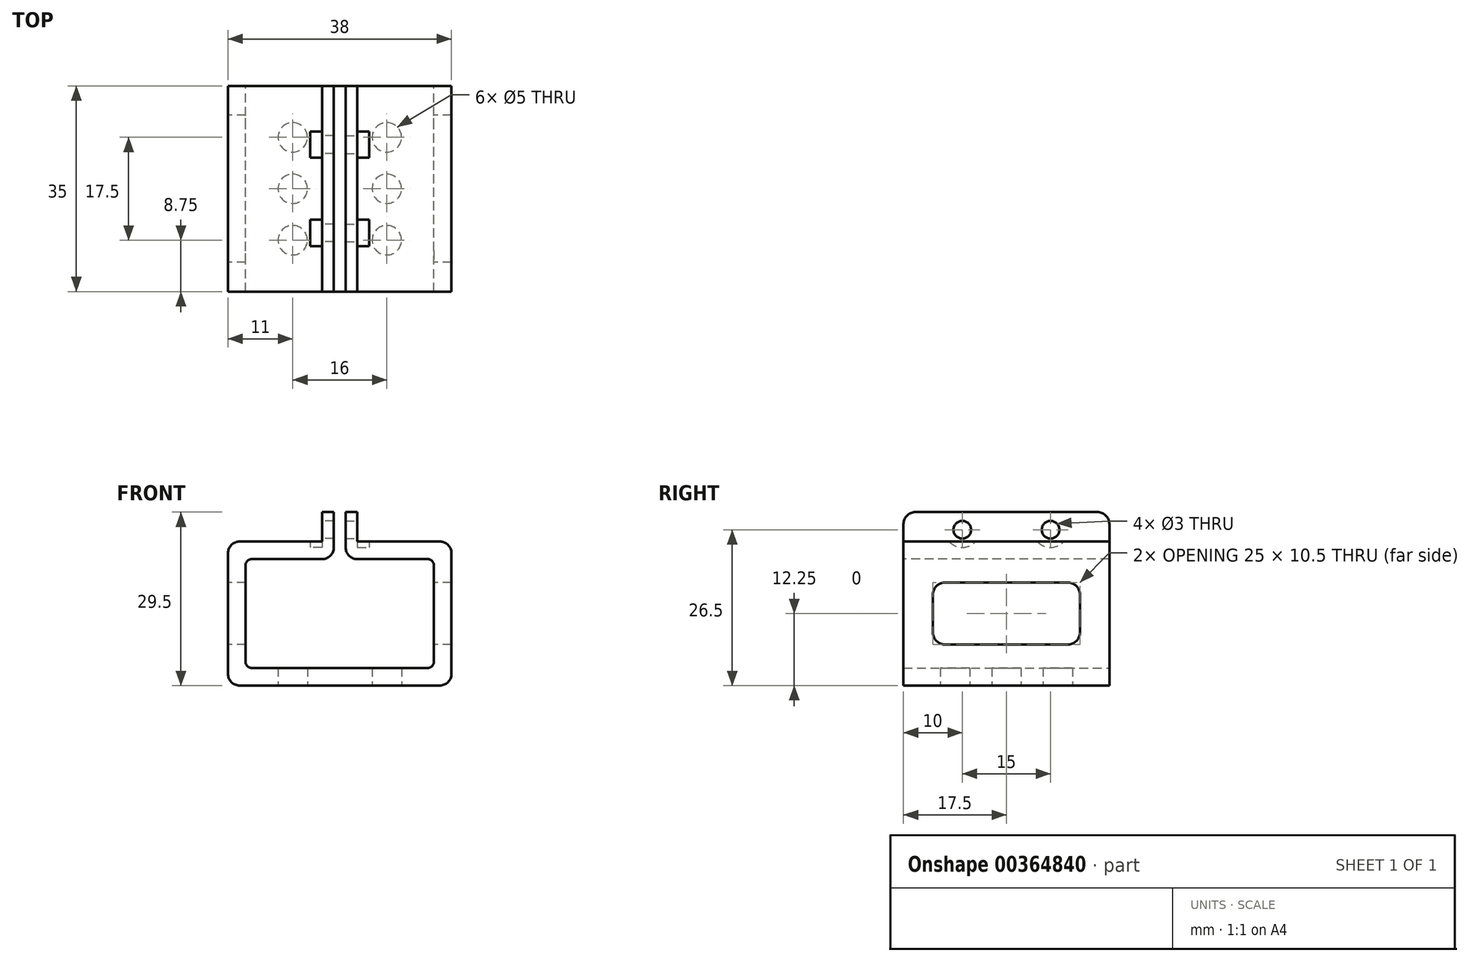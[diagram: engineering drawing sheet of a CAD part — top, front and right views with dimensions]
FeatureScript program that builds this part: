
annotation { "Feature Type Name" : "Feature", "Feature Type Description" : "" }
export const myFeature = defineFeature(function(context is Context, id is Id, definition is map)
    precondition{}
    {
        {
            var Q0;
            Q0=qCreatedBy(makeId("Front.planeOp"),FACE);
            var sketch = newSketch(context, id + "F0", { "sketchPlane" : qUnion([Q0])});
            skLineSegment(sketch, "E0.bottom", {"start": v(-16, 9.25) * mm, "end": v(16, 9.25) * mm});
            skLineSegment(sketch, "E0.top", {"start": v(-16, -9.25) * mm, "end": v(16, -9.25) * mm});
            skLineSegment(sketch, "E0.left", {"start": v(-16, 9.25) * mm, "end": v(-16, -9.25) * mm});
            skLineSegment(sketch, "E0.right", {"start": v(16, 9.25) * mm, "end": v(16, -9.25) * mm});
            skPoint(sketch, "E0.middle", {"position": v(0, 0) * mm});
            skLineSegment(sketch, "E1.0", {"start": v(-19, 12.25) * mm, "end": v(-19, -12.25) * mm});
            skLineSegment(sketch, "E1.1", {"start": v(-19, 12.25) * mm, "end": v(19, 12.25) * mm});
            skLineSegment(sketch, "E1.2", {"start": v(19, 12.25) * mm, "end": v(19, -12.25) * mm});
            skLineSegment(sketch, "E1.3", {"start": v(-19, -12.25) * mm, "end": v(19, -12.25) * mm});
            skSolve(sketch);
        }
        {
            var Q0;
            Q0=makeQuery(id+"F0.imprint","IMPRINT",FACE,{"disambiguationData":[TD([[makeQuery(id+"F0.imprint","IMPRINT",EDGE,{"derivedFrom":sQuery(id+"F0.wireOp",EDGE,"E0.bottom")}),1.0]])]});
            extrude(context, id + "F1", {"entities" : qUnion([Q0]), "depth" : 35 * mm});
        }
        {
            var Q0;
            Q0=makeQuery(id+"F1.opExtrude","SWEPT_EDGE",EDGE,{"disambiguationData":[OSD([sQuery(id+"F0.wireOp",EDGE,"E1.1"),sQuery(id+"F0.wireOp",EDGE,"E1.2")])]});
            var Q1;
            Q1=makeQuery(id+"F1.opExtrude","SWEPT_EDGE",EDGE,{"disambiguationData":[OSD([sQuery(id+"F0.wireOp",EDGE,"E1.2"),sQuery(id+"F0.wireOp",EDGE,"E1.3")])]});
            var Q2;
            Q2=makeQuery(id+"F1.opExtrude","SWEPT_EDGE",EDGE,{"disambiguationData":[OSD([sQuery(id+"F0.wireOp",EDGE,"E1.0"),sQuery(id+"F0.wireOp",EDGE,"E1.1")])]});
            var Q3;
            Q3=makeQuery(id+"F1.opExtrude","SWEPT_EDGE",EDGE,{"disambiguationData":[OSD([sQuery(id+"F0.wireOp",EDGE,"E1.0"),sQuery(id+"F0.wireOp",EDGE,"E1.3")])]});
            fillet(context, id + "F2", {"entities" : qUnion([Q0, Q1, Q2, Q3]), "radius" : 2 * mm, "tangentPropagation" : true, "allowEdgeOverflow" : false});
        }
        {
            var Q0;
            Q0=makeQuery(id+"F1.opExtrude","SWEPT_EDGE",EDGE,{"disambiguationData":[OSD([sQuery(id+"F0.wireOp",EDGE,"E0.bottom"),sQuery(id+"F0.wireOp",EDGE,"E0.left")])]});
            var Q1;
            Q1=makeQuery(id+"F1.opExtrude","SWEPT_EDGE",EDGE,{"disambiguationData":[OSD([sQuery(id+"F0.wireOp",EDGE,"E0.bottom"),sQuery(id+"F0.wireOp",EDGE,"E0.right")])]});
            var Q2;
            Q2=makeQuery(id+"F1.opExtrude","SWEPT_EDGE",EDGE,{"disambiguationData":[OSD([sQuery(id+"F0.wireOp",EDGE,"E0.top"),sQuery(id+"F0.wireOp",EDGE,"E0.right")])]});
            var Q3;
            Q3=makeQuery(id+"F1.opExtrude","SWEPT_EDGE",EDGE,{"disambiguationData":[OSD([sQuery(id+"F0.wireOp",EDGE,"E0.top"),sQuery(id+"F0.wireOp",EDGE,"E0.left")])]});
            fillet(context, id + "F3", {"entities" : qUnion([Q0, Q1, Q2, Q3]), "radius" : 1 * mm, "tangentPropagation" : true, "allowEdgeOverflow" : false});
        }
        {
            var Q0;
            Q0=makeQuery(id+"F1.opExtrude","CAP_FACE",FACE,{"disambiguationData":[OSD([sQuery(id+"F0.wireOp",EDGE,"E0.bottom"),sQuery(id+"F0.wireOp",EDGE,"E0.top"),sQuery(id+"F0.wireOp",EDGE,"E0.left"),sQuery(id+"F0.wireOp",EDGE,"E0.right"),sQuery(id+"F0.wireOp",EDGE,"E1.0"),sQuery(id+"F0.wireOp",EDGE,"E1.1"),sQuery(id+"F0.wireOp",EDGE,"E1.2"),sQuery(id+"F0.wireOp",EDGE,"E1.3")])],"isStart":false});
            var sketch = newSketch(context, id + "F4", { "sketchPlane" : qUnion([Q0])});
            skLineSegment(sketch, "E2.0", {"start": v(-19, 10.25) * mm, "end": v(-19, -10.25) * mm});
            skLineSegment(sketch, "E3.0", {"start": v(-17, 12.25) * mm, "end": v(17, 12.25) * mm});
            skLineSegment(sketch, "E4.0", {"start": v(19, 10.25) * mm, "end": v(19, -10.25) * mm});
            skLineSegment(sketch, "E5.0", {"start": v(10, 12.25) * mm, "end": v(10, -10.5) * mm});
            skLineSegment(sketch, "E6.0", {"start": v(-10, 12.25) * mm, "end": v(-10, -10.5) * mm});
            skLineSegment(sketch, "E7.0", {"start": v(-10, 9.25) * mm, "end": v(10, 9.25) * mm});
            skPoint(sketch, "E8.orphan", {"position": v(-15, 9.25) * mm});
            skPoint(sketch, "E9.orphan", {"position": v(15, 9.25) * mm});
            skSolve(sketch);
        }
        {
            var Q0;
            {var subQ5=sQuery(id+"F4.wireOp",EDGE,"E7.0");Q0=makeQuery(id+"F4.imprint","IMPRINT",FACE,{"disambiguationData":[TD([[makeQuery(id+"F4.imprint","IMPRINT",EDGE,{"derivedFrom":subQ5}),1.0]])]});}
            var Q1;
            Q1=qCreatedBy(makeId("Front.planeOp"),FACE);
            extrude(context, id + "F5", {"entities" : qUnion([Q0]), "operationType" : NewBodyOperationType.REMOVE, "endBound" : BoundingType.UP_TO_SURFACE, "oppositeDirection" : true, "endBoundEntityFace" : qUnion([Q1]), "depth" : 25 * mm});
        }
        {
            var Q0;
            Q0=makeQuery(id+"F1.opExtrude","SWEPT_FACE",FACE,{"disambiguationData":[OSD([sQuery(id+"F0.wireOp",EDGE,"E1.0")])]});
            var sketch = newSketch(context, id + "F6", { "sketchPlane" : qUnion([Q0])});
            skLineSegment(sketch, "E10.0.0", {"start": v(0, 10.25) * mm, "end": v(0, -10.25) * mm});
            skLineSegment(sketch, "E10.0.1", {"start": v(0, -10.25) * mm, "end": v(35, -10.25) * mm});
            skLineSegment(sketch, "E10.0.2", {"start": v(35, -10.25) * mm, "end": v(35, 10.25) * mm});
            skLineSegment(sketch, "E10.0.3", {"start": v(35, 10.25) * mm, "end": v(0, 10.25) * mm});
            skLineSegment(sketch, "E11.0", {"start": v(7, -5.25) * mm, "end": v(28, -5.25) * mm});
            skLineSegment(sketch, "E11.1", {"start": v(5, 3.25) * mm, "end": v(5, -3.25) * mm});
            skLineSegment(sketch, "E11.2", {"start": v(28, 5.25) * mm, "end": v(7, 5.25) * mm});
            skLineSegment(sketch, "E11.3", {"start": v(30, -3.25) * mm, "end": v(30, 3.25) * mm});
            skPoint(sketch, "E12.visualSharp", {"position": v(30, -5.25) * mm});
            skArc(sketch, "E12.filletArc", {"start": v(28, -5.25) * mm, "mid": v(29.41, -4.66) * mm, "end": v(30, -3.25) * mm});
            skPoint(sketch, "E13.visualSharp", {"position": v(5, -5.25) * mm});
            skArc(sketch, "E13.filletArc", {"start": v(5, -3.25) * mm, "mid": v(5.59, -4.66) * mm, "end": v(7, -5.25) * mm});
            skPoint(sketch, "E14.visualSharp", {"position": v(5, 5.25) * mm});
            skArc(sketch, "E14.filletArc", {"start": v(7, 5.25) * mm, "mid": v(5.59, 4.66) * mm, "end": v(5, 3.25) * mm});
            skPoint(sketch, "E15.visualSharp", {"position": v(30, 5.25) * mm});
            skArc(sketch, "E15.filletArc", {"start": v(30, 3.25) * mm, "mid": v(29.41, 4.66) * mm, "end": v(28, 5.25) * mm});
            skSolve(sketch);
        }
        {
            var Q0;
            Q0=makeQuery(id+"F6.imprint","IMPRINT",FACE,{"disambiguationData":[TD([[makeQuery(id+"F6.imprint","IMPRINT",EDGE,{"derivedFrom":sQuery(id+"F6.wireOp",EDGE,"E11.0")}),1.0]])]});
            var Q1;
            Q1=makeQuery(id+"F1.opExtrude","SWEPT_FACE",FACE,{"disambiguationData":[OSD([sQuery(id+"F0.wireOp",EDGE,"E1.2")])]});
            extrude(context, id + "F7", {"entities" : qUnion([Q0]), "operationType" : NewBodyOperationType.REMOVE, "endBound" : BoundingType.UP_TO_SURFACE, "oppositeDirection" : true, "endBoundEntityFace" : qUnion([Q1]), "depth" : 25 * mm});
        }
        {
            var Q0;
            Q0=makeQuery(id+"F1.opExtrude","SWEPT_FACE",FACE,{"disambiguationData":[OSD([sQuery(id+"F0.wireOp",EDGE,"E1.3")])]});
            var sketch = newSketch(context, id + "F8", { "sketchPlane" : qUnion([Q0])});
            skLineSegment(sketch, "E16.0", {"start": v(-17, 35) * mm, "end": v(-17, 0) * mm});
            skLineSegment(sketch, "E17.0", {"start": v(17, 0) * mm, "end": v(17, 35) * mm});
            skLineSegment(sketch, "E18.0", {"start": v(-17, 35) * mm, "end": v(17, 35) * mm});
            skLineSegment(sketch, "E19.0", {"start": v(-17, 0) * mm, "end": v(17, 0) * mm});
            skLineSegment(sketch, "E20.0", {"start": v(-8, 35) * mm, "end": v(-8, 0) * mm});
            skLineSegment(sketch, "E21.0", {"start": v(8, 0) * mm, "end": v(8, 35) * mm});
            skLineSegment(sketch, "E22.0", {"start": v(-17, 8.75) * mm, "end": v(17, 8.75) * mm});
            skLineSegment(sketch, "E23.0", {"start": v(-17, 17.5) * mm, "end": v(17, 17.5) * mm});
            skLineSegment(sketch, "E24.0", {"start": v(-17, 26.25) * mm, "end": v(17, 26.25) * mm});
            skPoint(sketch, "E25", {"position": v(-8, 26.25) * mm});
            skPoint(sketch, "E26", {"position": v(-8, 17.5) * mm});
            skPoint(sketch, "E27", {"position": v(-8, 8.75) * mm});
            skPoint(sketch, "E28", {"position": v(8, 26.25) * mm});
            skPoint(sketch, "E29", {"position": v(8, 17.5) * mm});
            skPoint(sketch, "E30", {"position": v(8, 8.75) * mm});
            skSolve(sketch);
        }
        {
            var Q0;
            Q0=sQuery(id+"F8.wireOp",VERTEX,"E25");
            var Q1;
            Q1=sQuery(id+"F8.wireOp",VERTEX,"E26");
            var Q2;
            Q2=sQuery(id+"F8.wireOp",VERTEX,"E27");
            var Q3;
            Q3=sQuery(id+"F8.wireOp",VERTEX,"E28");
            var Q4;
            Q4=sQuery(id+"F8.wireOp",VERTEX,"E29");
            var Q5;
            Q5=sQuery(id+"F8.wireOp",VERTEX,"E30");
            var Q6;
            Q6=makeQuery(id+"F1.opExtrude","SWEPT_BODY",BODY,{"disambiguationData":[OSD([sQuery(id+"F0.wireOp",EDGE,"E0.bottom"),sQuery(id+"F0.wireOp",EDGE,"E0.top"),sQuery(id+"F0.wireOp",EDGE,"E0.left"),sQuery(id+"F0.wireOp",EDGE,"E0.right"),sQuery(id+"F0.wireOp",EDGE,"E1.0"),sQuery(id+"F0.wireOp",EDGE,"E1.1"),sQuery(id+"F0.wireOp",EDGE,"E1.2"),sQuery(id+"F0.wireOp",EDGE,"E1.3")])]});
            hole(context, id + "F9", {"style" : HoleStyle.SIMPLE, "endStyle" : HoleEndStyle.BLIND, "holeDiameter" : 5 * mm, "holeDepth" : 3 * mm, "isTappedThrough" : true, "tappedDepth" : 12 * mm, "tapClearance" : 3, "locations" : qUnion([Q0, Q1, Q2, Q3, Q4, Q5]), "scope" : qUnion([Q6])});
        }
        {
            var Q0;
            Q0=makeQuery(id+"F1.opExtrude","CAP_FACE",FACE,{"disambiguationData":[OSD([sQuery(id+"F0.wireOp",EDGE,"E0.bottom"),sQuery(id+"F0.wireOp",EDGE,"E0.top"),sQuery(id+"F0.wireOp",EDGE,"E0.left"),sQuery(id+"F0.wireOp",EDGE,"E0.right"),sQuery(id+"F0.wireOp",EDGE,"E1.0"),sQuery(id+"F0.wireOp",EDGE,"E1.1"),sQuery(id+"F0.wireOp",EDGE,"E1.2"),sQuery(id+"F0.wireOp",EDGE,"E1.3")])],"isStart":false});
            var sketch = newSketch(context, id + "F10", { "sketchPlane" : qUnion([Q0])});
            skLineSegment(sketch, "E31.0", {"start": v(-17, 12.25) * mm, "end": v(-10, 12.25) * mm});
            skLineSegment(sketch, "E32.0", {"start": v(-15, 9.25) * mm, "end": v(-10, 9.25) * mm});
            skLineSegment(sketch, "E33.0", {"start": v(-10, 12.25) * mm, "end": v(-10, 9.25) * mm});
            skLineSegment(sketch, "E34.0", {"start": v(10, 12.25) * mm, "end": v(17, 12.25) * mm});
            skLineSegment(sketch, "E35.0", {"start": v(10, 12.25) * mm, "end": v(10, 9.25) * mm});
            skLineSegment(sketch, "E36.0", {"start": v(10, 9.25) * mm, "end": v(15, 9.25) * mm});
            skLineSegment(sketch, "E37.0", {"start": v(-1, 12.25) * mm, "end": v(-1, 9.25) * mm});
            skLineSegment(sketch, "E38.0", {"start": v(1, 12.25) * mm, "end": v(1, 9.25) * mm});
            skLineSegment(sketch, "E39", {"start": v(-10, 12.25) * mm, "end": v(-1, 12.25) * mm});
            skLineSegment(sketch, "E40", {"start": v(-10, 9.25) * mm, "end": v(-1, 9.25) * mm});
            skLineSegment(sketch, "E41", {"start": v(10, 12.25) * mm, "end": v(1, 12.25) * mm});
            skLineSegment(sketch, "E42", {"start": v(10, 9.25) * mm, "end": v(1, 9.25) * mm});
            skSolve(sketch);
        }
        {
            var Q0;
            Q0=makeQuery(id+"F10.imprint","IMPRINT",FACE,{"disambiguationData":[TD([[makeQuery(id+"F10.imprint","IMPRINT",EDGE,{"derivedFrom":sQuery(id+"F10.wireOp",EDGE,"E33.0")}),1.0]])]});
            var Q1;
            Q1=makeQuery(id+"F10.imprint","IMPRINT",FACE,{"disambiguationData":[TD([[makeQuery(id+"F10.imprint","IMPRINT",EDGE,{"derivedFrom":sQuery(id+"F10.wireOp",EDGE,"E35.0")}),-1.0]])]});
            var Q2;
            Q2=makeQuery(id+"F1.opExtrude","CAP_FACE",FACE,{"disambiguationData":[OSD([sQuery(id+"F0.wireOp",EDGE,"E0.bottom"),sQuery(id+"F0.wireOp",EDGE,"E0.top"),sQuery(id+"F0.wireOp",EDGE,"E0.left"),sQuery(id+"F0.wireOp",EDGE,"E0.right"),sQuery(id+"F0.wireOp",EDGE,"E1.0"),sQuery(id+"F0.wireOp",EDGE,"E1.1"),sQuery(id+"F0.wireOp",EDGE,"E1.2"),sQuery(id+"F0.wireOp",EDGE,"E1.3")])],"isStart":true});
            extrude(context, id + "F11", {"entities" : qUnion([Q0, Q1]), "operationType" : NewBodyOperationType.ADD, "endBound" : BoundingType.UP_TO_SURFACE, "oppositeDirection" : true, "endBoundEntityFace" : qUnion([Q2]), "depth" : 25 * mm});
        }
        {
            var Q0;
            Q0=makeQuery(id+"F11.boolean.opBoolean","MERGE",FACE,{"derivedFrom":[makeQuery(id+"F1.opExtrude","CAP_FACE",FACE,{"disambiguationData":[OSD([sQuery(id+"F0.wireOp",EDGE,"E0.bottom"),sQuery(id+"F0.wireOp",EDGE,"E0.top"),sQuery(id+"F0.wireOp",EDGE,"E0.left"),sQuery(id+"F0.wireOp",EDGE,"E0.right"),sQuery(id+"F0.wireOp",EDGE,"E1.0"),sQuery(id+"F0.wireOp",EDGE,"E1.1"),sQuery(id+"F0.wireOp",EDGE,"E1.2"),sQuery(id+"F0.wireOp",EDGE,"E1.3")])],"isStart":false}),makeQuery(id+"F11.opExtrude","CAP_FACE",FACE,{"disambiguationData":[OSD([sQuery(id+"F10.wireOp",EDGE,"E33.0"),sQuery(id+"F10.wireOp",EDGE,"E37.0"),sQuery(id+"F10.wireOp",EDGE,"E39"),sQuery(id+"F10.wireOp",EDGE,"E40")])],"isStart":true}),makeQuery(id+"F11.opExtrude","CAP_FACE",FACE,{"disambiguationData":[OSD([sQuery(id+"F10.wireOp",EDGE,"E35.0"),sQuery(id+"F10.wireOp",EDGE,"E38.0"),sQuery(id+"F10.wireOp",EDGE,"E41"),sQuery(id+"F10.wireOp",EDGE,"E42")])],"isStart":true})]});
            var sketch = newSketch(context, id + "F12", { "sketchPlane" : qUnion([Q0])});
            skLineSegment(sketch, "E43.0", {"start": v(-15, 9.25) * mm, "end": v(-1, 9.25) * mm});
            skLineSegment(sketch, "E44.0", {"start": v(-1, 17.25) * mm, "end": v(-1, 12.25) * mm});
            skLineSegment(sketch, "E45.0", {"start": v(-3, 17.25) * mm, "end": v(-3, 12.25) * mm});
            skLineSegment(sketch, "E46.0", {"start": v(-15, 17.25) * mm, "end": v(-1, 17.25) * mm});
            skLineSegment(sketch, "E47.0", {"start": v(0, 17.25) * mm, "end": v(0, 12.25) * mm});
            skLineSegment(sketch, "E48.MirrorCS", {"start": v(1, 17.25) * mm, "end": v(1, 12.25) * mm});
            skLineSegment(sketch, "E49.MirrorCS", {"start": v(3, 17.25) * mm, "end": v(3, 12.25) * mm});
            skLineSegment(sketch, "E50.MirrorCS", {"start": v(15, 17.25) * mm, "end": v(1, 17.25) * mm});
            skSolve(sketch);
        }
        {
            var Q0;
            {var subQ0=sQuery(id+"F12.wireOp",EDGE,"E44.0");Q0=makeQuery(id+"F12.imprint","IMPRINT",FACE,{"disambiguationData":[TD([[makeQuery(id+"F12.imprint","IMPRINT",EDGE,{"derivedFrom":subQ0}),-1.0]])]});}
            var Q1;
            {var subQ0=sQuery(id+"F12.wireOp",EDGE,"E48.MirrorCS");Q1=makeQuery(id+"F12.imprint","IMPRINT",FACE,{"disambiguationData":[TD([[makeQuery(id+"F12.imprint","IMPRINT",EDGE,{"derivedFrom":subQ0}),1.0]])]});}
            var Q2;
            Q2=makeQuery(id+"F11.boolean.opBoolean","MERGE",FACE,{"derivedFrom":[makeQuery(id+"F1.opExtrude","CAP_FACE",FACE,{"disambiguationData":[OSD([sQuery(id+"F0.wireOp",EDGE,"E0.bottom"),sQuery(id+"F0.wireOp",EDGE,"E0.top"),sQuery(id+"F0.wireOp",EDGE,"E0.left"),sQuery(id+"F0.wireOp",EDGE,"E0.right"),sQuery(id+"F0.wireOp",EDGE,"E1.0"),sQuery(id+"F0.wireOp",EDGE,"E1.1"),sQuery(id+"F0.wireOp",EDGE,"E1.2"),sQuery(id+"F0.wireOp",EDGE,"E1.3")])],"isStart":true}),makeQuery(id+"F11.opExtrude","CAP_FACE",FACE,{"disambiguationData":[OSD([sQuery(id+"F10.wireOp",EDGE,"E33.0"),sQuery(id+"F10.wireOp",EDGE,"E37.0"),sQuery(id+"F10.wireOp",EDGE,"E39"),sQuery(id+"F10.wireOp",EDGE,"E40")])],"isStart":false}),makeQuery(id+"F11.opExtrude","CAP_FACE",FACE,{"disambiguationData":[OSD([sQuery(id+"F10.wireOp",EDGE,"E35.0"),sQuery(id+"F10.wireOp",EDGE,"E38.0"),sQuery(id+"F10.wireOp",EDGE,"E41"),sQuery(id+"F10.wireOp",EDGE,"E42")])],"isStart":false})]});
            extrude(context, id + "F13", {"entities" : qUnion([Q0, Q1]), "operationType" : NewBodyOperationType.ADD, "endBound" : BoundingType.UP_TO_SURFACE, "oppositeDirection" : true, "endBoundEntityFace" : qUnion([Q2]), "depth" : 25 * mm});
        }
        {
            var Q0;
            Q0=makeQuery(id+"F13.opExtrude","CAP_EDGE",EDGE,{"disambiguationData":[OSD([sQuery(id+"F12.wireOp",EDGE,"E46.0")])],"isStart":true});
            var Q1;
            Q1=makeQuery(id+"F13.opExtrude","CAP_EDGE",EDGE,{"disambiguationData":[OSD([sQuery(id+"F12.wireOp",EDGE,"E50.MirrorCS")])],"isStart":true});
            var Q2;
            Q2=makeQuery(id+"F13.opExtrude","CAP_EDGE",EDGE,{"disambiguationData":[OSD([sQuery(id+"F12.wireOp",EDGE,"E46.0")])],"isStart":false});
            var Q3;
            Q3=makeQuery(id+"F13.opExtrude","CAP_EDGE",EDGE,{"disambiguationData":[OSD([sQuery(id+"F12.wireOp",EDGE,"E50.MirrorCS")])],"isStart":false});
            var Q4;
            Q4=makeQuery(id+"F13.opExtrude","SWEPT_EDGE",EDGE,{"disambiguationData":[OSD([sQuery(id+"F0.wireOp",EDGE,"E1.1"),sQuery(id+"F10.wireOp",EDGE,"E39"),sQuery(id+"F12.wireOp",EDGE,"E45.0")])]});
            var Q5;
            Q5=makeQuery(id+"F13.opExtrude","SWEPT_EDGE",EDGE,{"disambiguationData":[OSD([sQuery(id+"F0.wireOp",EDGE,"E1.1"),sQuery(id+"F10.wireOp",EDGE,"E41"),sQuery(id+"F12.wireOp",EDGE,"E49.MirrorCS")])]});
            fillet(context, id + "F14", {"entities" : qUnion([Q0, Q1, Q2, Q3, Q4, Q5]), "radius" : 2 * mm, "tangentPropagation" : true, "allowEdgeOverflow" : false});
        }
        {
            var Q0;
            Q0=makeQuery(id+"F13.opExtrude","SWEPT_FACE",FACE,{"disambiguationData":[OSD([sQuery(id+"F12.wireOp",EDGE,"E45.0")])]});
            var sketch = newSketch(context, id + "F15", { "sketchPlane" : qUnion([Q0])});
            skLineSegment(sketch, "E51.0", {"start": v(0, 14.25) * mm, "end": v(35, 14.25) * mm});
            skLineSegment(sketch, "E52.0", {"start": v(35, 15.25) * mm, "end": v(35, 14.25) * mm});
            skLineSegment(sketch, "E53.0", {"start": v(0, 14.25) * mm, "end": v(0, 15.25) * mm});
            skLineSegment(sketch, "E54.0", {"start": v(25, 15.25) * mm, "end": v(25, 14.25) * mm});
            skLineSegment(sketch, "E55.0", {"start": v(10, 14.25) * mm, "end": v(10, 15.25) * mm});
            skLineSegment(sketch, "E56.0", {"start": v(2, 17.25) * mm, "end": v(33, 17.25) * mm});
            skLineSegment(sketch, "E57.0", {"start": v(2, 14.25) * mm, "end": v(33, 14.25) * mm});
            skPoint(sketch, "E58", {"position": v(10, 14.25) * mm});
            skPoint(sketch, "E59", {"position": v(25, 14.25) * mm});
            skSolve(sketch);
        }
        {
            var Q0;
            {var subQ1=sQuery(id+"F15.wireOp",EDGE,"E52.0");Q0=makeQuery(id+"F15.imprint","IMPRINT",FACE,{"disambiguationData":[TD([[makeQuery(id+"F15.imprint","IMPRINT",EDGE,{"derivedFrom":subQ1}),-1.0]])]});}
            cPlane(context, id + "F16", {"entities" : qUnion([Q0]), "cplaneType" : CPlaneType.OFFSET, "offset" : 2 * mm, "width" : 150 * mm, "height" : 150 * mm});
        }
        {
            var Q0;
            Q0=qCreatedBy(id+"F16.planeOp",FACE);
            var sketch = newSketch(context, id + "F17", { "sketchPlane" : qUnion([Q0])});
            skPoint(sketch, "E60.0", {"position": v(10, 14.25) * mm});
            skPoint(sketch, "E61.0", {"position": v(25, 14.25) * mm});
            skSolve(sketch);
        }
        {
            var Q0;
            Q0=sQuery(id+"F17.wireOp",VERTEX,"E60.0");
            var Q1;
            Q1=sQuery(id+"F17.wireOp",VERTEX,"E61.0");
            var Q2;
            Q2=makeQuery(id+"F1.opExtrude","SWEPT_BODY",BODY,{"disambiguationData":[OSD([sQuery(id+"F0.wireOp",EDGE,"E0.bottom"),sQuery(id+"F0.wireOp",EDGE,"E0.top"),sQuery(id+"F0.wireOp",EDGE,"E0.left"),sQuery(id+"F0.wireOp",EDGE,"E0.right"),sQuery(id+"F0.wireOp",EDGE,"E1.0"),sQuery(id+"F0.wireOp",EDGE,"E1.1"),sQuery(id+"F0.wireOp",EDGE,"E1.2"),sQuery(id+"F0.wireOp",EDGE,"E1.3")])]});
            hole(context, id + "F18", {"style" : HoleStyle.C_BORE, "endStyle" : HoleEndStyle.BLIND, "holeDiameter" : 3 * mm, "cBoreDiameter" : 6 * mm, "cBoreDepth" : 2 * mm, "holeDepth" : 4 * mm, "isTappedThrough" : true, "tappedDepth" : 12 * mm, "tapClearance" : 3, "locations" : qUnion([Q0, Q1]), "scope" : qUnion([Q2])});
        }
        {
            var Q0;
            Q0=makeQuery(id+"F13.opExtrude","SWEPT_FACE",FACE,{"disambiguationData":[OSD([sQuery(id+"F12.wireOp",EDGE,"E49.MirrorCS")])]});
            cPlane(context, id + "F19", {"entities" : qUnion([Q0]), "cplaneType" : CPlaneType.OFFSET, "offset" : 2 * mm, "width" : 150 * mm, "height" : 150 * mm});
        }
        {
            var Q0;
            Q0=qCreatedBy(id+"F19.planeOp",FACE);
            var sketch = newSketch(context, id + "F20", { "sketchPlane" : qUnion([Q0])});
            skPoint(sketch, "E62.0", {"position": v(-25, 14.25) * mm});
            skPoint(sketch, "E63.0", {"position": v(-10, 14.25) * mm});
            skSolve(sketch);
        }
        {
            var Q0;
            Q0=sQuery(id+"F20.wireOp",VERTEX,"E62.0");
            var Q1;
            Q1=sQuery(id+"F20.wireOp",VERTEX,"E63.0");
            var Q2;
            Q2=makeQuery(id+"F1.opExtrude","SWEPT_BODY",BODY,{"disambiguationData":[OSD([sQuery(id+"F0.wireOp",EDGE,"E0.bottom"),sQuery(id+"F0.wireOp",EDGE,"E0.top"),sQuery(id+"F0.wireOp",EDGE,"E0.left"),sQuery(id+"F0.wireOp",EDGE,"E0.right"),sQuery(id+"F0.wireOp",EDGE,"E1.0"),sQuery(id+"F0.wireOp",EDGE,"E1.1"),sQuery(id+"F0.wireOp",EDGE,"E1.2"),sQuery(id+"F0.wireOp",EDGE,"E1.3")])]});
            hole(context, id + "F21", {"style" : HoleStyle.C_BORE, "endStyle" : HoleEndStyle.BLIND, "holeDiameter" : 3 * mm, "cBoreDiameter" : 6 * mm, "cBoreDepth" : 2 * mm, "holeDepth" : 4 * mm, "isTappedThrough" : true, "tappedDepth" : 12 * mm, "tapClearance" : 3, "locations" : qUnion([Q0, Q1]), "scope" : qUnion([Q2])});
        }
        {
            var Q0;
            Q0=makeQuery(id+"F11.opExtrude","SWEPT_EDGE",EDGE,{"disambiguationData":[OSD([sQuery(id+"F10.wireOp",EDGE,"E37.0"),sQuery(id+"F10.wireOp",EDGE,"E40")])]});
            var Q1;
            Q1=makeQuery(id+"F11.opExtrude","SWEPT_EDGE",EDGE,{"disambiguationData":[OSD([sQuery(id+"F10.wireOp",EDGE,"E38.0"),sQuery(id+"F10.wireOp",EDGE,"E42")])]});
            fillet(context, id + "F22", {"entities" : qUnion([Q0, Q1]), "radius" : 2 * mm, "tangentPropagation" : true, "allowEdgeOverflow" : false});
        }
    });
